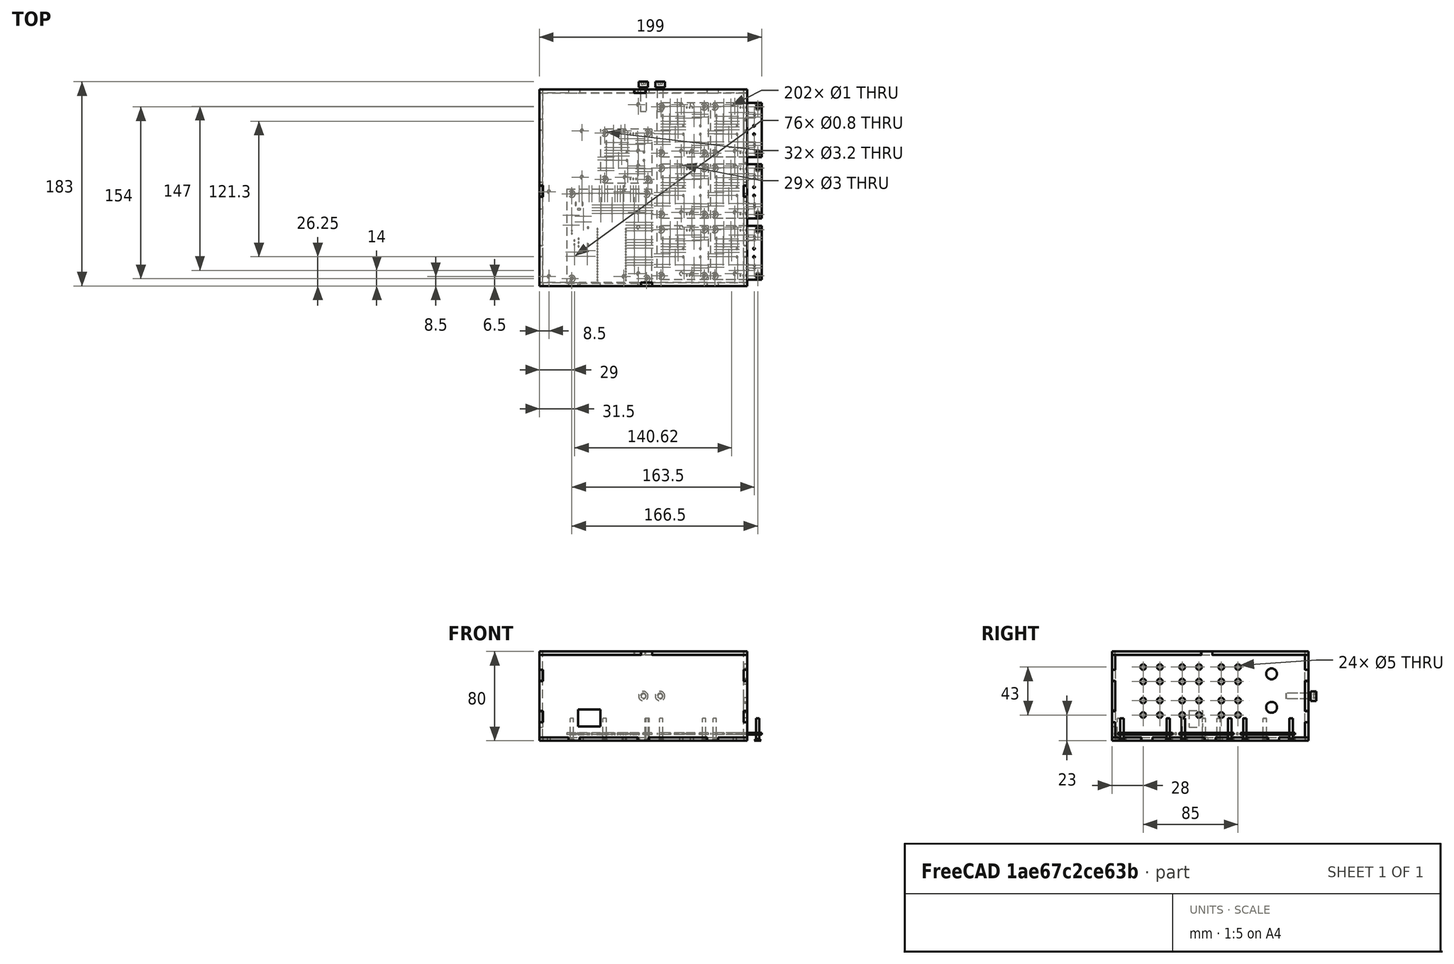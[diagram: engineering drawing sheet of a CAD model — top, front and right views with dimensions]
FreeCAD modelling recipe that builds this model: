
FCSTD DOCUMENT  (FreeCAD 0.20R29177 +426 (Git))
Label: multi_join_preview
License: All rights reserved
LicenseURL: http://en.wikipedia.org/wiki/All_rights_reserved
objects: Part::Feature×74, Part::Cylinder×35, App::LinkGroup×15, Part::Compound×13, Part::Cut×7, Part::Box×2
note: 131 computed .brp shape members not serialized (recipe doc carries the construction recipe); baked Part::Feature solids carry a one-line shape summary decoded from their .brp

FEATURE [Part::Feature] face_panel_tab
  shape: bbox 186 x 3 x 80 mm, 60 faces (baked)
FEATURE [Part::Feature] behind_panel_tab
  shape: bbox 186 x 3 x 80 mm, 60 faces (baked)
FEATURE [Part::Feature] left_panel_tab
  shape: bbox 3 x 176 x 80 mm, 56 faces (baked)
FEATURE [Part::Feature] right_panel_tab
  shape: bbox 3 x 176 x 80 mm, 56 faces (baked)
FEATURE [Part::Feature] bottom_panel_tab
  shape: bbox 186 x 176 x 3 mm, 90 faces (baked)
FEATURE [Part::Feature] top_panel_tab
  shape: bbox 186 x 176 x 3 mm, 32 faces (baked)
FEATURE [Part::Cylinder] Cylinder
  Angle = 360
  AttacherType = Attacher::AttachEngine3D
  FirstAngle = 0
  Height = 20
  Placement = pos=(79,55,-10.12) rot=(0,1,0;1.5708rad)
  Radius = 4.88
  SecondAngle = 0
FEATURE [Part::Cylinder] Cylinder001
  Angle = 360
  AttacherType = Attacher::AttachEngine3D
  FirstAngle = 0
  Height = 20
  Placement = pos=(79,55,19.88) rot=(0,1,0;1.5708rad)
  Radius = 4.88
  SecondAngle = 0
FEATURE [Part::Feature] BOLTS_part036  label="Hex socket head cap screw DIN 912 M5 20.0"
  Placement = pos=(15,95,0) rot=(1,0,0;1.5708rad)
  shape: bbox 8.5 x 27 x 8.5 mm, 12 faces (baked)
FEATURE [Part::Feature] BOLTS_part037  label="Hex socket head cap screw DIN 912 M5 20.001"
  Placement = pos=(0,95,0) rot=(1,0,0;1.5708rad)
  shape: bbox 8.5 x 27 x 8.5 mm, 12 faces (baked)
FEATURE [Part::Feature] BOLTS_part038  label="Hex socket head cap screw DIN 912 M5 20.002"
  Placement = pos=(15,95,0) rot=(1,0,0;1.5708rad)
  shape: bbox 8.5 x 27 x 8.5 mm, 12 faces (baked)
FEATURE [Part::Feature] BOLTS_part039  label="Hex socket head cap screw DIN 912 M5 20.003"
  Placement = pos=(0,95,0) rot=(1,0,0;1.5708rad)
  shape: bbox 8.5 x 27 x 8.5 mm, 12 faces (baked)
FEATURE [Part::Feature] BOLTS_part040  label="Hex socket head cap screw DIN 912 M5 20.004"
  Placement = pos=(15,95,0) rot=(1,0,0;1.5708rad)
  shape: bbox 8.5 x 27 x 8.5 mm, 12 faces (baked)
FEATURE [Part::Feature] BOLTS_part041  label="Hex socket head cap screw DIN 912 M5 20.005"
  Placement = pos=(0,95,0) rot=(1,0,0;1.5708rad)
  shape: bbox 8.5 x 27 x 8.5 mm, 12 faces (baked)
FEATURE [Part::Feature] BOLTS_part042  label="Hex socket head cap screw DIN 912 M5 20.006"
  Placement = pos=(15,95,0) rot=(1,0,0;1.5708rad)
  shape: bbox 8.5 x 27 x 8.5 mm, 12 faces (baked)
FEATURE [Part::Feature] BOLTS_part043  label="Hex socket head cap screw DIN 912 M5 20.007"
  Placement = pos=(0,95,0) rot=(1,0,0;1.5708rad)
  shape: bbox 8.5 x 27 x 8.5 mm, 12 faces (baked)
FEATURE [Part::Feature] BOLTS_part044  label="Hex socket head cap screw DIN 912 M5 20.008"
  Placement = pos=(15,95,0) rot=(1,0,0;1.5708rad)
  shape: bbox 8.5 x 27 x 8.5 mm, 12 faces (baked)
FEATURE [Part::Feature] BOLTS_part045  label="Hex socket head cap screw DIN 912 M5 20.009"
  Placement = pos=(0,95,0) rot=(1,0,0;1.5708rad)
  shape: bbox 8.5 x 27 x 8.5 mm, 12 faces (baked)
FEATURE [Part::Feature] BOLTS_part046  label="Hex socket head cap screw DIN 912 M5 20.010"
  Placement = pos=(15,95,0) rot=(1,0,0;1.5708rad)
  shape: bbox 8.5 x 27 x 8.5 mm, 12 faces (baked)
FEATURE [Part::Feature] BOLTS_part047  label="Hex socket head cap screw DIN 912 M5 20.011"
  Placement = pos=(0,95,0) rot=(1,0,0;1.5708rad)
  shape: bbox 8.5 x 27 x 8.5 mm, 12 faces (baked)
FEATURE [Part::Feature] BOLTS_part048  label="Hex socket head cap screw DIN 912 M5 20.012"
  Placement = pos=(15,95,0) rot=(1,0,0;1.5708rad)
  shape: bbox 8.5 x 27 x 8.5 mm, 12 faces (baked)
FEATURE [Part::Feature] BOLTS_part049  label="Hex socket head cap screw DIN 912 M5 20.013"
  Placement = pos=(0,95,0) rot=(1,0,0;1.5708rad)
  shape: bbox 8.5 x 27 x 8.5 mm, 12 faces (baked)
FEATURE [Part::Feature] BOLTS_part050  label="Hex socket head cap screw DIN 912 M5 20.014"
  Placement = pos=(15,95,0) rot=(1,0,0;1.5708rad)
  shape: bbox 8.5 x 27 x 8.5 mm, 12 faces (baked)
FEATURE [Part::Feature] BOLTS_part051  label="Hex socket head cap screw DIN 912 M5 20.015"
  Placement = pos=(0,95,0) rot=(1,0,0;1.5708rad)
  shape: bbox 8.5 x 27 x 8.5 mm, 12 faces (baked)
FEATURE [Part::Feature] BOLTS_part052  label="Hex socket head cap screw DIN 912 M5 20.016"
  Placement = pos=(15,95,0) rot=(1,0,0;1.5708rad)
  shape: bbox 8.5 x 27 x 8.5 mm, 12 faces (baked)
FEATURE [Part::Feature] BOLTS_part053  label="Hex socket head cap screw DIN 912 M5 20.017"
  Placement = pos=(0,95,0) rot=(1,0,0;1.5708rad)
  shape: bbox 8.5 x 27 x 8.5 mm, 12 faces (baked)
FEATURE [Part::Feature] BOLTS_part054  label="Hex socket head cap screw DIN 912 M5 20.018"
  Placement = pos=(15,95,0) rot=(1,0,0;1.5708rad)
  shape: bbox 8.5 x 27 x 8.5 mm, 12 faces (baked)
FEATURE [Part::Feature] BOLTS_part055  label="Hex socket head cap screw DIN 912 M5 20.019"
  Placement = pos=(0,95,0) rot=(1,0,0;1.5708rad)
  shape: bbox 8.5 x 27 x 8.5 mm, 12 faces (baked)
FEATURE [Part::Feature] BOLTS_part056  label="Hex socket head cap screw DIN 912 M5 20.020"
  Placement = pos=(15,95,0) rot=(1,0,0;1.5708rad)
  shape: bbox 8.5 x 27 x 8.5 mm, 12 faces (baked)
FEATURE [Part::Feature] BOLTS_part057  label="Hex socket head cap screw DIN 912 M5 20.021"
  Placement = pos=(0,95,0) rot=(1,0,0;1.5708rad)
  shape: bbox 8.5 x 27 x 8.5 mm, 12 faces (baked)
FEATURE [Part::Feature] BOLTS_part058  label="Hex socket head cap screw DIN 912 M5 20.022"
  Placement = pos=(15,95,0) rot=(1,0,0;1.5708rad)
  shape: bbox 8.5 x 27 x 8.5 mm, 12 faces (baked)
FEATURE [Part::Feature] BOLTS_part059  label="Hex socket head cap screw DIN 912 M5 20.023"
  Placement = pos=(0,95,0) rot=(1,0,0;1.5708rad)
  shape: bbox 8.5 x 27 x 8.5 mm, 12 faces (baked)
FEATURE [Part::Box] Box001  label="Cube"
  AttacherType = Attacher::AttachEngine3D
  Height = 15
  Length = 20
  Placement = pos=(-58.5,-94.26,-27.17) rot=(0,0,1;0rad)
  Width = 20
FEATURE [Part::Box] Box002  label="Cube001"
  AttacherType = Attacher::AttachEngine3D
  Height = 15
  Length = 20
  Placement = pos=(-96,-19,-28) rot=(0,0,1;0rad)
  Width = 12
FEATURE [App::LinkGroup] LinkGroup001  label="banana_plugs1"
  ElementList = -> [BOLTS_part036,BOLTS_part037]
  LinkMode = 0
FEATURE [App::LinkGroup] LinkGroup002  label="banana_plugs002"
  ElementList = -> [BOLTS_part038,BOLTS_part039]
  LinkMode = 0
  Placement = pos=(35,0,0) rot=(0,0,1;0rad)
FEATURE [App::LinkGroup] LinkGroup003  label="banana_plugs003"
  ElementList = -> [BOLTS_part040,BOLTS_part041]
  LinkMode = 0
  Placement = pos=(35,0,-13) rot=(0,0,1;0rad)
FEATURE [App::LinkGroup] LinkGroup004  label="banana_plugs004"
  ElementList = -> [BOLTS_part042,BOLTS_part043]
  LinkMode = 0
  Placement = pos=(0,0,-13) rot=(0,0,1;0rad)
FEATURE [App::LinkGroup] LinkGroup005  label="banana_plugs005"
  ElementList = -> [BOLTS_part044,BOLTS_part045]
  LinkMode = 0
  Placement = pos=(-35,0,0) rot=(0,0,1;0rad)
FEATURE [App::LinkGroup] LinkGroup006  label="banana_plugs006"
  ElementList = -> [BOLTS_part046,BOLTS_part047]
  LinkMode = 0
  Placement = pos=(-35,0,-13) rot=(0,0,1;0rad)
FEATURE [App::LinkGroup] LinkGroup007
  ElementList = -> [LinkGroup001,LinkGroup002,LinkGroup003,LinkGroup004,LinkGroup005,LinkGroup006]
  LinkMode = 0
  Placement = pos=(4,-10,26) rot=(0,0,1;-1.5708rad)
FEATURE [App::LinkGroup] LinkGroup008  label="banana_plugs007"
  ElementList = -> [BOLTS_part048,BOLTS_part049]
  LinkMode = 0
FEATURE [App::LinkGroup] LinkGroup009  label="banana_plugs008"
  ElementList = -> [BOLTS_part050,BOLTS_part051]
  LinkMode = 0
  Placement = pos=(35,0,0) rot=(0,0,1;0rad)
FEATURE [App::LinkGroup] LinkGroup010  label="banana_plugs009"
  ElementList = -> [BOLTS_part052,BOLTS_part053]
  LinkMode = 0
  Placement = pos=(35,0,-13) rot=(0,0,1;0rad)
FEATURE [App::LinkGroup] LinkGroup011  label="banana_plugs010"
  ElementList = -> [BOLTS_part054,BOLTS_part055]
  LinkMode = 0
  Placement = pos=(0,0,-13) rot=(0,0,1;0rad)
FEATURE [App::LinkGroup] LinkGroup012  label="banana_plugs011"
  ElementList = -> [BOLTS_part056,BOLTS_part057]
  LinkMode = 0
  Placement = pos=(-35,0,0) rot=(0,0,1;0rad)
FEATURE [App::LinkGroup] LinkGroup013  label="banana_plugs012"
  ElementList = -> [BOLTS_part058,BOLTS_part059]
  LinkMode = 0
  Placement = pos=(-35,0,-13) rot=(0,0,1;0rad)
FEATURE [App::LinkGroup] LinkGroup014
  ElementList = -> [LinkGroup008,LinkGroup009,LinkGroup010,LinkGroup011,LinkGroup012,LinkGroup013]
  LinkMode = 0
  Placement = pos=(4,-10,-4) rot=(0,0,1;-1.5708rad)
FEATURE [Part::Feature] BOLTS_part  label="Hex socket countersunk head screw DIN 7991 M3 20.0"
  Placement = pos=(16,-79,-40) rot=(0,0,1;0rad)
  shape: bbox 6 x 6 x 20 mm, 12 faces (baked)
FEATURE [Part::Feature] BOLTS_part001  label="Hex socket countersunk head screw DIN 7991 M3 20.001"
  Placement = pos=(16,-37.5,-40) rot=(0,0,1;0rad)
  shape: bbox 6 x 6 x 20 mm, 12 faces (baked)
FEATURE [Part::Feature] BOLTS_part002  label="Hex socket countersunk head screw DIN 7991 M3 20.002"
  Placement = pos=(54.5,-37.5,-40) rot=(0,0,1;0rad)
  shape: bbox 6 x 6 x 20 mm, 12 faces (baked)
FEATURE [Part::Feature] BOLTS_part003  label="Hex socket countersunk head screw DIN 7991 M3 20.003"
  Placement = pos=(54.5,-79,-40) rot=(0,0,1;0rad)
  shape: bbox 6 x 6 x 20 mm, 12 faces (baked)
FEATURE [Part::Feature] BOLTS_part004  label="Hex socket countersunk head screw DIN 7991 M3 20.004"
  Placement = pos=(16,-79,-40) rot=(0,0,1;0rad)
  shape: bbox 6 x 6 x 20 mm, 12 faces (baked)
FEATURE [Part::Feature] BOLTS_part005  label="Hex socket countersunk head screw DIN 7991 M3 20.005"
  Placement = pos=(16,-37.5,-40) rot=(0,0,1;0rad)
  shape: bbox 6 x 6 x 20 mm, 12 faces (baked)
FEATURE [Part::Feature] BOLTS_part006  label="Hex socket countersunk head screw DIN 7991 M3 20.006"
  Placement = pos=(54.5,-37.5,-40) rot=(0,0,1;0rad)
  shape: bbox 6 x 6 x 20 mm, 12 faces (baked)
FEATURE [Part::Feature] BOLTS_part007  label="Hex socket countersunk head screw DIN 7991 M3 20.007"
  Placement = pos=(54.5,-79,-40) rot=(0,0,1;0rad)
  shape: bbox 6 x 6 x 20 mm, 12 faces (baked)
FEATURE [Part::Feature] BOLTS_part008  label="Hex socket countersunk head screw DIN 7991 M3 20.008"
  Placement = pos=(16,-79,-40) rot=(0,0,1;0rad)
  shape: bbox 6 x 6 x 20 mm, 12 faces (baked)
FEATURE [Part::Feature] BOLTS_part009  label="Hex socket countersunk head screw DIN 7991 M3 20.009"
  Placement = pos=(16,-37.5,-40) rot=(0,0,1;0rad)
  shape: bbox 6 x 6 x 20 mm, 12 faces (baked)
FEATURE [Part::Feature] BOLTS_part010  label="Hex socket countersunk head screw DIN 7991 M3 20.010"
  Placement = pos=(54.5,-37.5,-40) rot=(0,0,1;0rad)
  shape: bbox 6 x 6 x 20 mm, 12 faces (baked)
FEATURE [Part::Feature] BOLTS_part011  label="Hex socket countersunk head screw DIN 7991 M3 20.011"
  Placement = pos=(54.5,-79,-40) rot=(0,0,1;0rad)
  shape: bbox 6 x 6 x 20 mm, 12 faces (baked)
FEATURE [Part::Feature] BOLTS_part012  label="Hex socket countersunk head screw DIN 7991 M3 20.012"
  Placement = pos=(16,-79,-40) rot=(0,0,1;0rad)
  shape: bbox 6 x 6 x 20 mm, 12 faces (baked)
FEATURE [Part::Feature] BOLTS_part013  label="Hex socket countersunk head screw DIN 7991 M3 20.013"
  Placement = pos=(16,-37.5,-40) rot=(0,0,1;0rad)
  shape: bbox 6 x 6 x 20 mm, 12 faces (baked)
FEATURE [Part::Feature] BOLTS_part014  label="Hex socket countersunk head screw DIN 7991 M3 20.014"
  Placement = pos=(54.5,-37.5,-40) rot=(0,0,1;0rad)
  shape: bbox 6 x 6 x 20 mm, 12 faces (baked)
FEATURE [Part::Feature] BOLTS_part015  label="Hex socket countersunk head screw DIN 7991 M3 20.015"
  Placement = pos=(54.5,-79,-40) rot=(0,0,1;0rad)
  shape: bbox 6 x 6 x 20 mm, 12 faces (baked)
FEATURE [Part::Feature] BOLTS_part016  label="Hex socket countersunk head screw DIN 7991 M3 20.016"
  Placement = pos=(16,-79,-40) rot=(0,0,1;0rad)
  shape: bbox 6 x 6 x 20 mm, 12 faces (baked)
FEATURE [Part::Feature] BOLTS_part017  label="Hex socket countersunk head screw DIN 7991 M3 20.017"
  Placement = pos=(16,-37.5,-40) rot=(0,0,1;0rad)
  shape: bbox 6 x 6 x 20 mm, 12 faces (baked)
FEATURE [Part::Feature] BOLTS_part018  label="Hex socket countersunk head screw DIN 7991 M3 20.018"
  Placement = pos=(54.5,-37.5,-40) rot=(0,0,1;0rad)
  shape: bbox 6 x 6 x 20 mm, 12 faces (baked)
FEATURE [Part::Feature] BOLTS_part019  label="Hex socket countersunk head screw DIN 7991 M3 20.019"
  Placement = pos=(54.5,-79,-40) rot=(0,0,1;0rad)
  shape: bbox 6 x 6 x 20 mm, 12 faces (baked)
FEATURE [Part::Feature] BOLTS_part020  label="Hex socket countersunk head screw DIN 7991 M3 20.020"
  Placement = pos=(16,-79,-40) rot=(0,0,1;0rad)
  shape: bbox 6 x 6 x 20 mm, 12 faces (baked)
FEATURE [Part::Feature] BOLTS_part021  label="Hex socket countersunk head screw DIN 7991 M3 20.021"
  Placement = pos=(16,-37.5,-40) rot=(0,0,1;0rad)
  shape: bbox 6 x 6 x 20 mm, 12 faces (baked)
FEATURE [Part::Feature] BOLTS_part022  label="Hex socket countersunk head screw DIN 7991 M3 20.022"
  Placement = pos=(54.5,-37.5,-40) rot=(0,0,1;0rad)
  shape: bbox 6 x 6 x 20 mm, 12 faces (baked)
FEATURE [Part::Feature] BOLTS_part023  label="Hex socket countersunk head screw DIN 7991 M3 20.023"
  Placement = pos=(54.5,-79,-40) rot=(0,0,1;0rad)
  shape: bbox 6 x 6 x 20 mm, 12 faces (baked)
FEATURE [Part::Feature] BOLTS_part024  label="Hex socket countersunk head screw DIN 7991 M3 20.024"
  Placement = pos=(16,-79,-40) rot=(0,0,1;0rad)
  shape: bbox 6 x 6 x 20 mm, 12 faces (baked)
FEATURE [Part::Feature] BOLTS_part025  label="Hex socket countersunk head screw DIN 7991 M3 20.025"
  Placement = pos=(16,-37.5,-40) rot=(0,0,1;0rad)
  shape: bbox 6 x 6 x 20 mm, 12 faces (baked)
FEATURE [Part::Feature] BOLTS_part026  label="Hex socket countersunk head screw DIN 7991 M3 20.026"
  Placement = pos=(54.5,-37.5,-40) rot=(0,0,1;0rad)
  shape: bbox 6 x 6 x 20 mm, 12 faces (baked)
FEATURE [Part::Feature] BOLTS_part027  label="Hex socket countersunk head screw DIN 7991 M3 20.027"
  Placement = pos=(54.5,-79,-40) rot=(0,0,1;0rad)
  shape: bbox 6 x 6 x 20 mm, 12 faces (baked)
FEATURE [Part::Feature] BOLTS_part028  label="Hex socket countersunk head screw DIN 7991 M3 20.028"
  Placement = pos=(3,-81.5,-53) rot=(0,0,1;0rad)
  shape: bbox 6 x 6 x 20 mm, 12 faces (baked)
FEATURE [Part::Feature] BOLTS_part029  label="Hex socket countersunk head screw DIN 7991 M3 20.029"
  Placement = pos=(3,-5.5,-53) rot=(0,0,1;0rad)
  shape: bbox 6 x 6 x 20 mm, 12 faces (baked)
FEATURE [Part::Feature] BOLTS_part030  label="Hex socket countersunk head screw DIN 7991 M3 20.030"
  Placement = pos=(-64,-81.5,-53) rot=(0,0,1;0rad)
  shape: bbox 6 x 6 x 20 mm, 12 faces (baked)
FEATURE [Part::Feature] BOLTS_part031  label="Hex socket countersunk head screw DIN 7991 M3 20.031"
  Placement = pos=(-64,-5.5,-53) rot=(0,0,1;0rad)
  shape: bbox 6 x 6 x 20 mm, 12 faces (baked)
FEATURE [Part::Feature] BOLTS_part032  label="Hex socket countersunk head screw DIN 7991 M3 20.032"
  Placement = pos=(16,-79,-40) rot=(0,0,1;0rad)
  shape: bbox 6 x 6 x 20 mm, 12 faces (baked)
FEATURE [Part::Feature] BOLTS_part033  label="Hex socket countersunk head screw DIN 7991 M3 20.033"
  Placement = pos=(16,-37.5,-40) rot=(0,0,1;0rad)
  shape: bbox 6 x 6 x 20 mm, 12 faces (baked)
FEATURE [Part::Feature] BOLTS_part034  label="Hex socket countersunk head screw DIN 7991 M3 20.034"
  Placement = pos=(54.5,-37.5,-40) rot=(0,0,1;0rad)
  shape: bbox 6 x 6 x 20 mm, 12 faces (baked)
FEATURE [Part::Feature] BOLTS_part035  label="Hex socket countersunk head screw DIN 7991 M3 20.035"
  Placement = pos=(54.5,-79,-40) rot=(0,0,1;0rad)
  shape: bbox 6 x 6 x 20 mm, 12 faces (baked)
FEATURE [Part::Compound] Compound001  label="sol_driver_screw_Compound"
  Links = -> [BOLTS_part,BOLTS_part001,BOLTS_part002,BOLTS_part003]
  Placement = pos=(0,110,0) rot=(0,0,1;0rad)
FEATURE [Part::Compound] Compound002  label="sol_driver_screw_Compound001"
  Links = -> [BOLTS_part004,BOLTS_part005,BOLTS_part006,BOLTS_part007]
  Placement = pos=(0,55,0) rot=(0,0,1;0rad)
FEATURE [Part::Compound] Compound003  label="sol_driver_screw_Compound002"
  Links = -> [BOLTS_part008,BOLTS_part009,BOLTS_part010,BOLTS_part011]
FEATURE [Part::Compound] Compound005  label="sol_driver_screw_Compound003"
  Links = -> [BOLTS_part012,BOLTS_part013,BOLTS_part014,BOLTS_part015]
  Placement = pos=(0,110,0) rot=(0,0,1;0rad)
FEATURE [Part::Compound] Compound006  label="sol_driver_screw_Compound004"
  Links = -> [BOLTS_part016,BOLTS_part017,BOLTS_part018,BOLTS_part019]
  Placement = pos=(0,55,0) rot=(0,0,1;0rad)
FEATURE [Part::Compound] Compound007  label="sol_driver_screw_Compound005"
  Links = -> [BOLTS_part020,BOLTS_part021,BOLTS_part022,BOLTS_part023]
FEATURE [Part::Compound] Compound009  label="sol_driver_screw_Compound006"
  Links = -> [BOLTS_part024,BOLTS_part025,BOLTS_part026,BOLTS_part027]
FEATURE [Part::Compound] Compound010
  Links = -> [BOLTS_part028,BOLTS_part029,BOLTS_part030,BOLTS_part031]
  Placement = pos=(0,0,13) rot=(0,0,1;0rad)
FEATURE [Part::Compound] Compound011  label="sol_driver_screw_Compound007"
  Links = -> [BOLTS_part032,BOLTS_part033,BOLTS_part034,BOLTS_part035]
  Placement = pos=(-50.5,86.5,0) rot=(0,0,1;0rad)
FEATURE [Part::Cylinder] Cylinder002
  Angle = 360
  AttacherType = Attacher::AttachEngine3D
  FirstAngle = 0
  Height = 10
  Placement = pos=(82,74.5,-47) rot=(0,0,1;0rad)
  Radius = 1.5
  SecondAngle = 0
FEATURE [Part::Cylinder] Cylinder004
  Angle = 360
  AttacherType = Attacher::AttachEngine3D
  FirstAngle = 0
  Height = 10
  Placement = pos=(82,33,-47) rot=(0,0,1;0rad)
  Radius = 1.5
  SecondAngle = 0
FEATURE [Part::Cylinder] Cylinder005
  Angle = 360
  AttacherType = Attacher::AttachEngine3D
  FirstAngle = 0
  Height = 10
  Placement = pos=(43.5,33,-47) rot=(0,0,1;0rad)
  Radius = 1.5
  SecondAngle = 0
FEATURE [Part::Cylinder] Cylinder006
  Angle = 360
  AttacherType = Attacher::AttachEngine3D
  FirstAngle = 0
  Height = 10
  Placement = pos=(82,19.5,-47) rot=(0,0,1;0rad)
  Radius = 1.5
  SecondAngle = 0
FEATURE [Part::Cylinder] Cylinder007
  Angle = 360
  AttacherType = Attacher::AttachEngine3D
  FirstAngle = 0
  Height = 10
  Placement = pos=(43.5,19.5,-47) rot=(0,0,1;0rad)
  Radius = 1.5
  SecondAngle = 0
FEATURE [Part::Cylinder] Cylinder008
  Angle = 360
  AttacherType = Attacher::AttachEngine3D
  FirstAngle = 0
  Height = 10
  Placement = pos=(82,-22,-47) rot=(0,0,1;0rad)
  Radius = 1.5
  SecondAngle = 0
FEATURE [Part::Cylinder] Cylinder009
  Angle = 360
  AttacherType = Attacher::AttachEngine3D
  FirstAngle = 0
  Height = 10
  Placement = pos=(43.5,-22,-47) rot=(0,0,1;0rad)
  Radius = 1.5
  SecondAngle = 0
FEATURE [Part::Cylinder] Cylinder010
  Angle = 360
  AttacherType = Attacher::AttachEngine3D
  FirstAngle = 0
  Height = 10
  Placement = pos=(82,-35.5,-47) rot=(0,0,1;0rad)
  Radius = 1.5
  SecondAngle = 0
FEATURE [Part::Cylinder] Cylinder012
  Angle = 360
  AttacherType = Attacher::AttachEngine3D
  FirstAngle = 0
  Height = 10
  Placement = pos=(43.5,-77,-47) rot=(0,0,1;0rad)
  Radius = 1.5
  SecondAngle = 0
FEATURE [Part::Cylinder] Cylinder013
  Angle = 360
  AttacherType = Attacher::AttachEngine3D
  FirstAngle = 0
  Height = 10
  Placement = pos=(82,-77,-47) rot=(0,0,1;0rad)
  Radius = 1.5
  SecondAngle = 0
FEATURE [Part::Cylinder] Cylinder014
  Angle = 360
  AttacherType = Attacher::AttachEngine3D
  FirstAngle = 0
  Height = 10
  Placement = pos=(43.5,-35.5,-47) rot=(0,0,1;0rad)
  Radius = 1.5
  SecondAngle = 0
FEATURE [Part::Cylinder] Cylinder015
  Angle = 360
  AttacherType = Attacher::AttachEngine3D
  FirstAngle = 0
  Height = 10
  Placement = pos=(34,-22,-47) rot=(0,0,1;0rad)
  Radius = 1.5
  SecondAngle = 0
FEATURE [Part::Cylinder] Cylinder016
  Angle = 360
  AttacherType = Attacher::AttachEngine3D
  FirstAngle = 0
  Height = 10
  Placement = pos=(-4.5,-77,-47) rot=(0,0,1;0rad)
  Radius = 1.5
  SecondAngle = 0
FEATURE [Part::Cylinder] Cylinder017
  Angle = 360
  AttacherType = Attacher::AttachEngine3D
  FirstAngle = 0
  Height = 10
  Placement = pos=(-17.5,-3.5,-47) rot=(0,0,1;0rad)
  Radius = 1.5
  SecondAngle = 0
FEATURE [Part::Cylinder] Cylinder018
  Angle = 360
  AttacherType = Attacher::AttachEngine3D
  FirstAngle = 0
  Height = 10
  Placement = pos=(-4.5,-22,-47) rot=(0,0,1;0rad)
  Radius = 1.5
  SecondAngle = 0
FEATURE [Part::Cylinder] Cylinder019
  Angle = 360
  AttacherType = Attacher::AttachEngine3D
  FirstAngle = 0
  Height = 10
  Placement = pos=(-17.5,-79.5,-47) rot=(0,0,1;0rad)
  Radius = 1.5
  SecondAngle = 0
FEATURE [Part::Cylinder] Cylinder020
  Angle = 360
  AttacherType = Attacher::AttachEngine3D
  FirstAngle = 0
  Height = 10
  Placement = pos=(34,19.5,-47) rot=(0,0,1;0rad)
  Radius = 1.5
  SecondAngle = 0
FEATURE [Part::Cylinder] Cylinder021
  Angle = 360
  AttacherType = Attacher::AttachEngine3D
  FirstAngle = 0
  Height = 10
  Placement = pos=(-16.5,9.5,-47) rot=(0,0,1;0rad)
  Radius = 1.5
  SecondAngle = 0
FEATURE [Part::Cylinder] Cylinder022
  Angle = 360
  AttacherType = Attacher::AttachEngine3D
  FirstAngle = 0
  Height = 10
  Placement = pos=(-84.5,-79.5,-47) rot=(0,0,1;0rad)
  Radius = 1.5
  SecondAngle = 0
FEATURE [Part::Cylinder] Cylinder023
  Angle = 360
  AttacherType = Attacher::AttachEngine3D
  FirstAngle = 0
  Height = 10
  Placement = pos=(-4.5,19.5,-47) rot=(0,0,1;0rad)
  Radius = 1.5
  SecondAngle = 0
FEATURE [Part::Cylinder] Cylinder024
  Angle = 360
  AttacherType = Attacher::AttachEngine3D
  FirstAngle = 0
  Height = 10
  Placement = pos=(-4.5,33,-47) rot=(0,0,1;0rad)
  Radius = 1.5
  SecondAngle = 0
FEATURE [Part::Cylinder] Cylinder025
  Angle = 360
  AttacherType = Attacher::AttachEngine3D
  FirstAngle = 0
  Height = 10
  Placement = pos=(34,33,-47) rot=(0,0,1;0rad)
  Radius = 1.5
  SecondAngle = 0
FEATURE [Part::Cylinder] Cylinder026
  Angle = 360
  AttacherType = Attacher::AttachEngine3D
  FirstAngle = 0
  Height = 10
  Placement = pos=(34,74.5,-47) rot=(0,0,1;0rad)
  Radius = 1.5
  SecondAngle = 0
FEATURE [Part::Cylinder] Cylinder027
  Angle = 360
  AttacherType = Attacher::AttachEngine3D
  FirstAngle = 0
  Height = 10
  Placement = pos=(-55,9.5,-47) rot=(0,0,1;0rad)
  Radius = 1.5
  SecondAngle = 0
FEATURE [Part::Cylinder] Cylinder028
  Angle = 360
  AttacherType = Attacher::AttachEngine3D
  FirstAngle = 0
  Height = 10
  Placement = pos=(-84.5,-3.5,-47) rot=(0,0,1;0rad)
  Radius = 1.5
  SecondAngle = 0
FEATURE [Part::Cylinder] Cylinder029
  Angle = 360
  AttacherType = Attacher::AttachEngine3D
  FirstAngle = 0
  Height = 10
  Placement = pos=(-55,51,-47) rot=(0,0,1;0rad)
  Radius = 1.5
  SecondAngle = 0
FEATURE [Part::Cylinder] Cylinder030
  Angle = 360
  AttacherType = Attacher::AttachEngine3D
  FirstAngle = 0
  Height = 10
  Placement = pos=(-16.5,51,-47) rot=(0,0,1;0rad)
  Radius = 1.5
  SecondAngle = 0
FEATURE [Part::Cylinder] Cylinder031
  Angle = 360
  AttacherType = Attacher::AttachEngine3D
  FirstAngle = 0
  Height = 10
  Placement = pos=(-4.5,74.5,-47) rot=(0,0,1;0rad)
  Radius = 1.5
  SecondAngle = 0
FEATURE [Part::Cylinder] Cylinder032
  Angle = 360
  AttacherType = Attacher::AttachEngine3D
  FirstAngle = 0
  Height = 10
  Placement = pos=(-84.5,-3.5,-47) rot=(0,0,1;0rad)
  Radius = 1.5
  SecondAngle = 0
FEATURE [Part::Cylinder] Cylinder033
  Angle = 360
  AttacherType = Attacher::AttachEngine3D
  FirstAngle = 0
  Height = 10
  Placement = pos=(43.5,74.5,-47.1) rot=(0,0,1;0rad)
  Radius = 1.5
  SecondAngle = 0
FEATURE [Part::Cylinder] Cylinder034
  Angle = 360
  AttacherType = Attacher::AttachEngine3D
  FirstAngle = 0
  Height = 10
  Placement = pos=(-4.5,-35.5,-47.1) rot=(0,0,1;0rad)
  Radius = 1.5
  SecondAngle = 0
FEATURE [Part::Cylinder] Cylinder035
  Angle = 360
  AttacherType = Attacher::AttachEngine3D
  FirstAngle = 0
  Height = 10
  Placement = pos=(34,-35.5,-47.1) rot=(0,0,1;0rad)
  Radius = 1.5
  SecondAngle = 0
FEATURE [Part::Cylinder] Cylinder036
  Angle = 360
  AttacherType = Attacher::AttachEngine3D
  FirstAngle = 0
  Height = 10
  Placement = pos=(34,-77,-47.1) rot=(0,0,1;0rad)
  Radius = 1.5
  SecondAngle = 0
FEATURE [Part::Feature] Pcb_b27c
  Placement = pos=(242,-190,0) rot=(0,0,1;3.14159rad)
  shape: bbox 76 x 85 x 1.6 mm, 143 faces (baked)
FEATURE [Part::Feature] Pcb_e13b
  Placement = pos=(0,112.5,0) rot=(0,0,1;0rad)
  shape: bbox 45.5 x 48.5 x 1.6 mm, 54 faces (baked)
FEATURE [Part::Feature] Pcb_e13b001
  Placement = pos=(0,57.5,0) rot=(0,0,1;0rad)
  shape: bbox 45.5 x 48.5 x 1.6 mm, 54 faces (baked)
FEATURE [Part::Feature] Pcb_e13b002
  Placement = pos=(0,2.5,0) rot=(0,0,1;0rad)
  shape: bbox 45.5 x 48.5 x 1.6 mm, 54 faces (baked)
FEATURE [Part::Compound] Compound  label="PCBs_Compound"
  Links = -> [Pcb_e13b,Pcb_e13b001,Pcb_e13b002,Pcb_b27c]
  Placement = pos=(-99.5,44,-33) rot=(0,0,1;0rad)
FEATURE [Part::Feature] Pcb_e13b003
  Placement = pos=(0,112.5,0) rot=(0,0,1;0rad)
  shape: bbox 45.5 x 48.5 x 1.6 mm, 54 faces (baked)
FEATURE [Part::Feature] Pcb_e13b004
  Placement = pos=(0,57.5,0) rot=(0,0,1;0rad)
  shape: bbox 45.5 x 48.5 x 1.6 mm, 54 faces (baked)
FEATURE [Part::Feature] Pcb_e13b005
  Placement = pos=(0,2.5,0) rot=(0,0,1;0rad)
  shape: bbox 45.5 x 48.5 x 1.6 mm, 54 faces (baked)
FEATURE [Part::Compound] Compound004  label="PCBs_Compound001"
  Links = -> [Pcb_e13b003,Pcb_e13b004,Pcb_e13b005]
  Placement = pos=(-99.5,44,-33) rot=(0,0,1;0rad)
FEATURE [Part::Compound] Compound008
  Links = -> [Compound007,Compound004,Compound005,Compound006]
  Placement = pos=(48,0,0) rot=(0,0,1;0rad)
FEATURE [Part::Feature] Pcb_e13b006
  Placement = pos=(-150,133,-33) rot=(0,0,1;0rad)
  shape: bbox 45.5 x 48.5 x 1.6 mm, 54 faces (baked)
FEATURE [App::LinkGroup] LinkGroup
  ElementList = -> [Compound,Compound001,Compound002,Compound003,Compound008,Compound009,Compound010,Pcb_e13b006,Compound011]
  LinkMode = 0
  Placement = pos=(-20.5,2,-0.1) rot=(0,0.999201,0.039968;0rad)
FEATURE [Part::Cut] Cut
  Base = -> left_panel_tab
  Tool = -> LinkGroup007
FEATURE [Part::Cut] Cut001
  Base = -> Cut
  Tool = -> LinkGroup014
FEATURE [Part::Cut] Cut002
  Base = -> Cut001
  Tool = -> Cylinder
FEATURE [Part::Cut] Cut003  label="left_panel_tab001"
  Base = -> Cut002
  Tool = -> Cylinder001
FEATURE [Part::Cut] Cut004  label="behind_panel"
  Base = -> behind_panel_tab
  Tool = -> Box001
FEATURE [Part::Cut] Cut005  label="right_panel"
  Base = -> right_panel_tab
  Tool = -> Box002
FEATURE [Part::Compound] Compound012
  Links = -> [Cylinder036,Cylinder002,Cylinder004,Cylinder005,Cylinder006,Cylinder007,Cylinder008,Cylinder009,Cylinder010,Cylinder012,Cylinder013,Cylinder014,Cylinder015,Cylinder016,Cylinder017,Cylinder018,Cylinder019,Cylinder020,Cylinder021,Cylinder022,Cylinder023,Cylinder024,Cylinder025,Cylinder026,Cylinder027,Cylinder028,Cylinder029,Cylinder030,Cylinder031,Cylinder032,Cylinder033,Cylinder034,Cylinder035]
FEATURE [Part::Cut] Cut006  label="bottom_panel"
  Base = -> bottom_panel_tab
  Tool = -> Compound012
